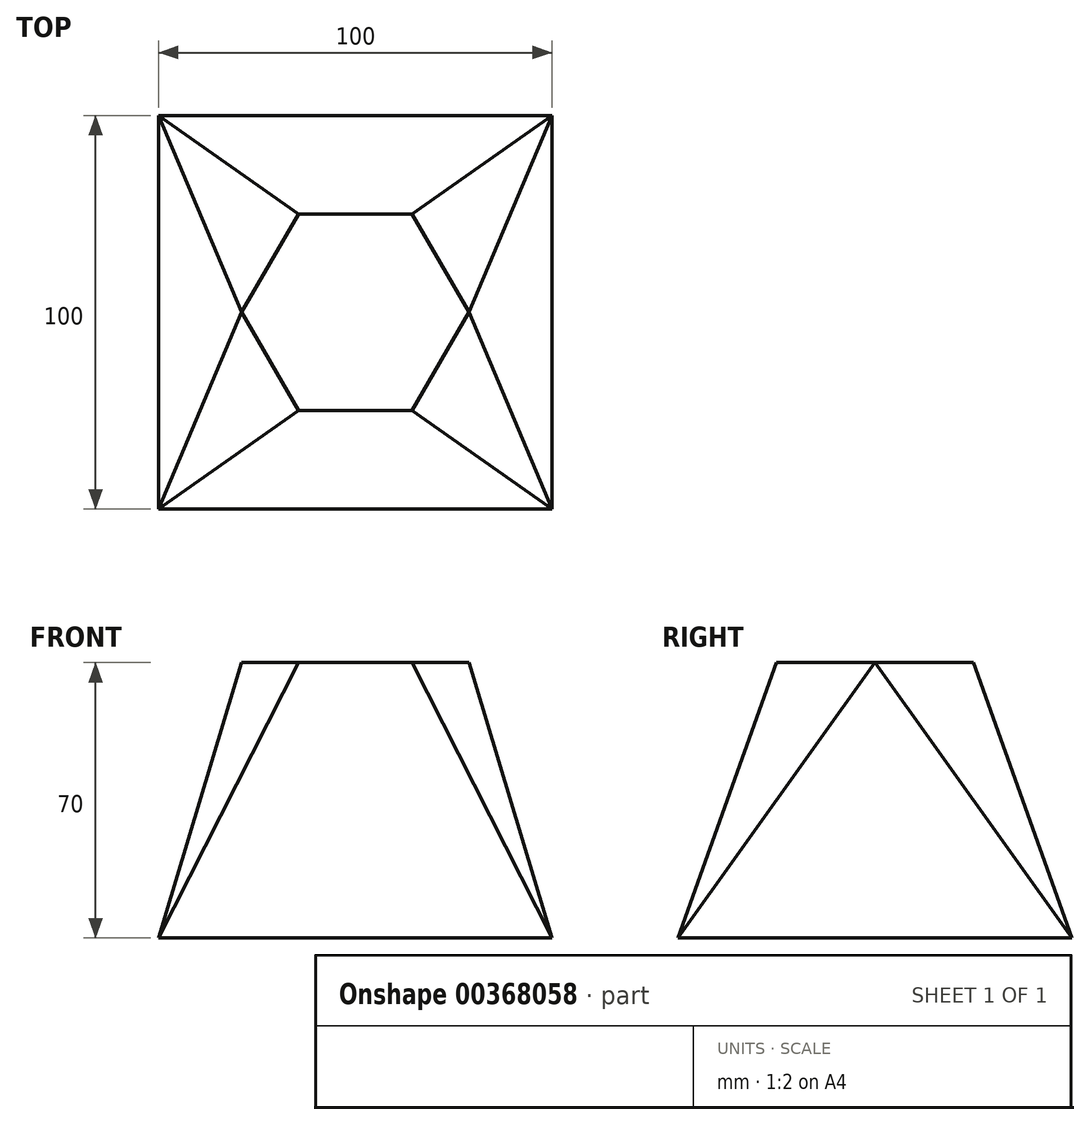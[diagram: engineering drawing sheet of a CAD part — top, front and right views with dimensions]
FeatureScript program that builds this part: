
annotation { "Feature Type Name" : "Feature", "Feature Type Description" : "" }
export const myFeature = defineFeature(function(context is Context, id is Id, definition is map)
    precondition{}
    {
        {
            var Q0;
            Q0=qCreatedBy(makeId("Top.planeOp"),FACE);
            var sketch = newSketch(context, id + "F0", { "sketchPlane" : qUnion([Q0])});
            skLineSegment(sketch, "E0.bottom", {"start": v(-50, 50) * mm, "end": v(50, 50) * mm});
            skLineSegment(sketch, "E0.top", {"start": v(-50, -50) * mm, "end": v(50, -50) * mm});
            skLineSegment(sketch, "E0.left", {"start": v(-50, 50) * mm, "end": v(-50, -50) * mm});
            skLineSegment(sketch, "E0.right", {"start": v(50, 50) * mm, "end": v(50, -50) * mm});
            skPoint(sketch, "E0.middle", {"position": v(0, 0) * mm});
            skSolve(sketch);
        }
        {
            var Q0;
            Q0=qCreatedBy(makeId("Top.planeOp"),FACE);
            cPlane(context, id + "F1", {"entities" : qUnion([Q0]), "cplaneType" : CPlaneType.OFFSET, "offset" : 70 * mm, "width" : 150 * mm, "height" : 150 * mm});
        }
        {
            var Q0;
            Q0=qCreatedBy(id+"F1.planeOp",FACE);
            var sketch = newSketch(context, id + "F2", { "sketchPlane" : qUnion([Q0])});
            skCircle(sketch, "E1.cCircle", {"center": v(0, 0) * mm, "radius": 25 * mm, "construction": true});
            skLineSegment(sketch, "E1.0", {"start": v(-14.43, 25) * mm, "end": v(14.43, 25) * mm});
            skLineSegment(sketch, "E1.1", {"start": v(14.43, 25) * mm, "end": v(28.87, 0) * mm});
            skLineSegment(sketch, "E1.2", {"start": v(28.87, 0) * mm, "end": v(14.43, -25) * mm});
            skLineSegment(sketch, "E1.3", {"start": v(14.43, -25) * mm, "end": v(-14.43, -25) * mm});
            skLineSegment(sketch, "E1.4", {"start": v(-14.43, -25) * mm, "end": v(-28.87, 0) * mm});
            skLineSegment(sketch, "E1.5", {"start": v(-28.87, 0) * mm, "end": v(-14.43, 25) * mm});
            skPoint(sketch, "E1.0.midPoint", {"position": v(0, 25) * mm});
            skLineSegment(sketch, "E2", {"start": v(-14.43, 25) * mm, "end": v(-14.43, -25) * mm});
            skLineSegment(sketch, "E3", {"start": v(14.43, 25) * mm, "end": v(14.43, -25) * mm});
            skSolve(sketch);
        }
        {
            var Q0;
            Q0=makeQuery(id+"F0.imprint","IMPRINT",FACE,{"disambiguationData":[TD([[makeQuery(id+"F0.imprint","IMPRINT",EDGE,{"derivedFrom":sQuery(id+"F0.wireOp",EDGE,"E0.bottom")}),-1.0]])]});
            var Q1;
            Q1=makeQuery(id+"F2.imprint","IMPRINT",FACE,{"disambiguationData":[TD([[makeQuery(id+"F2.imprint","IMPRINT",EDGE,{"derivedFrom":sQuery(id+"F2.wireOp",EDGE,"E1.0")}),-1.0]])]});
            loft(context, id + "F3", {"sheetProfilesArray" : [{ "sheetProfileEntities" : qUnion([Q0]) }, { "sheetProfileEntities" : qUnion([Q1]) }]});
        }
        {
            var Q1;
            Q1=makeQuery(id+"F2.imprint","IMPRINT",FACE,{"disambiguationData":[TD([[makeQuery(id+"F2.imprint","IMPRINT",EDGE,{"derivedFrom":sQuery(id+"F2.wireOp",EDGE,"E1.4")}),-1.0]])]});
            var Q2;
            Q2=makeQuery(id+"F3.opLoft","MID_CAP_VERTEX",VERTEX,{"disambiguationData":[OSD([sQuery(id+"F0.wireOp",EDGE,"E0.bottom"),sQuery(id+"F0.wireOp",EDGE,"E0.left")])],"capPos":0.0});
            loft(context, id + "F4", {"operationType" : NewBodyOperationType.ADD, "sheetProfilesArray" : [{ "sheetProfileEntities" : qUnion([Q1]) }, { "sheetProfileEntities" : qUnion([Q2]) }]});
        }
        {
            var Q1;
            Q1=makeQuery(id+"F2.imprint","IMPRINT",FACE,{"disambiguationData":[TD([[makeQuery(id+"F2.imprint","IMPRINT",EDGE,{"derivedFrom":sQuery(id+"F2.wireOp",EDGE,"E1.4")}),-1.0]])]});
            var Q2;
            Q2=makeQuery(id+"F3.opLoft","MID_CAP_VERTEX",VERTEX,{"disambiguationData":[OSD([sQuery(id+"F0.wireOp",EDGE,"E0.top"),sQuery(id+"F0.wireOp",EDGE,"E0.left")])],"capPos":0.0});
            loft(context, id + "F5", {"operationType" : NewBodyOperationType.ADD, "sheetProfilesArray" : [{ "sheetProfileEntities" : qUnion([Q1]) }, { "sheetProfileEntities" : qUnion([Q2]) }]});
        }
        {
            var Q1;
            Q1=makeQuery(id+"F4.opLoft","SWEPT_FACE",FACE,{"disambiguationData":[OSD([sQuery(id+"F2.wireOp",EDGE,"E1.3"),sQuery(id+"F2.wireOp",EDGE,"E1.4"),sQuery(id+"F2.wireOp",EDGE,"E1.5"),sQuery(id+"F2.wireOp",EDGE,"E2")])]});
            var Q2;
            Q2=makeQuery(id+"F5.opLoft","SWEPT_FACE",FACE,{"disambiguationData":[OSD([sQuery(id+"F2.wireOp",EDGE,"E1.0"),sQuery(id+"F2.wireOp",EDGE,"E1.4"),sQuery(id+"F2.wireOp",EDGE,"E1.5"),sQuery(id+"F2.wireOp",EDGE,"E2")])]});
            var Q3;
            {var subQ0=sQuery(id+"F0.wireOp",EDGE,"E0.left");var subQ1=sQuery(id+"F0.wireOp",EDGE,"E0.bottom");Q3=makeQuery(id+"F4.boolean.opBoolean","MERGE",VERTEX,{"derivedFrom":[makeQuery(id+"F3.opLoft","MID_CAP_VERTEX",VERTEX,{"disambiguationData":[OSD([subQ1,subQ0])],"capPos":0.0}),makeQuery(id+"F4.opLoft","SWEPT_VERTEX",VERTEX,{"disambiguationData":[OSD([subQ1,subQ0,sQuery(id+"F2.wireOp",EDGE,"E1.3"),sQuery(id+"F2.wireOp",EDGE,"E1.4"),sQuery(id+"F2.wireOp",EDGE,"E2")])]})]});}
            var Q4;
            {var subQ0=sQuery(id+"F0.wireOp",EDGE,"E0.left");var subQ1=sQuery(id+"F0.wireOp",EDGE,"E0.top");Q4=makeQuery(id+"F5.boolean.opBoolean","MERGE",VERTEX,{"derivedFrom":[makeQuery(id+"F3.opLoft","MID_CAP_VERTEX",VERTEX,{"disambiguationData":[OSD([subQ1,subQ0])],"capPos":0.0}),makeQuery(id+"F5.opLoft","SWEPT_VERTEX",VERTEX,{"disambiguationData":[OSD([subQ1,subQ0,sQuery(id+"F2.wireOp",EDGE,"E1.3"),sQuery(id+"F2.wireOp",EDGE,"E1.4"),sQuery(id+"F2.wireOp",EDGE,"E2")])]})]});}
            loft(context, id + "F6", {"operationType" : NewBodyOperationType.ADD, "sheetProfilesArray" : [{ "sheetProfileEntities" : qUnion([Q1]) }, { "sheetProfileEntities" : qUnion([Q2]) }], "matchConnections" : true, "connections" : [{ "connectionEntities" : qUnion([Q3, Q4]), "connectionEdgeQueries" : qUnion([]), "connectionEdgeParameters" : [] }]});
        }
        {
            var Q1;
            Q1=makeQuery(id+"F2.imprint","IMPRINT",FACE,{"disambiguationData":[TD([[makeQuery(id+"F2.imprint","IMPRINT",EDGE,{"derivedFrom":sQuery(id+"F2.wireOp",EDGE,"E1.1")}),-1.0]])]});
            var Q2;
            Q2=makeQuery(id+"F3.opLoft","MID_CAP_VERTEX",VERTEX,{"disambiguationData":[OSD([sQuery(id+"F0.wireOp",EDGE,"E0.top"),sQuery(id+"F0.wireOp",EDGE,"E0.right")])],"capPos":0.0});
            loft(context, id + "F7", {"operationType" : NewBodyOperationType.ADD, "sheetProfilesArray" : [{ "sheetProfileEntities" : qUnion([Q1]) }, { "sheetProfileEntities" : qUnion([Q2]) }]});
        }
        {
            var Q1;
            Q1=makeQuery(id+"F2.imprint","IMPRINT",FACE,{"disambiguationData":[TD([[makeQuery(id+"F2.imprint","IMPRINT",EDGE,{"derivedFrom":sQuery(id+"F2.wireOp",EDGE,"E1.1")}),-1.0]])]});
            var Q2;
            Q2=makeQuery(id+"F3.opLoft","MID_CAP_VERTEX",VERTEX,{"disambiguationData":[OSD([sQuery(id+"F0.wireOp",EDGE,"E0.bottom"),sQuery(id+"F0.wireOp",EDGE,"E0.right")])],"capPos":0.0});
            loft(context, id + "F8", {"operationType" : NewBodyOperationType.ADD, "sheetProfilesArray" : [{ "sheetProfileEntities" : qUnion([Q1]) }, { "sheetProfileEntities" : qUnion([Q2]) }]});
        }
        {
            var Q1;
            Q1=makeQuery(id+"F7.opLoft","SWEPT_FACE",FACE,{"disambiguationData":[OSD([sQuery(id+"F2.wireOp",EDGE,"E1.0"),sQuery(id+"F2.wireOp",EDGE,"E1.1"),sQuery(id+"F2.wireOp",EDGE,"E1.2"),sQuery(id+"F2.wireOp",EDGE,"E3")])]});
            var Q2;
            Q2=makeQuery(id+"F8.opLoft","SWEPT_FACE",FACE,{"disambiguationData":[OSD([sQuery(id+"F2.wireOp",EDGE,"E1.1"),sQuery(id+"F2.wireOp",EDGE,"E1.2"),sQuery(id+"F2.wireOp",EDGE,"E1.3"),sQuery(id+"F2.wireOp",EDGE,"E3")])]});
            var Q3;
            {var subQ0=sQuery(id+"F0.wireOp",EDGE,"E0.right");var subQ1=sQuery(id+"F0.wireOp",EDGE,"E0.top");Q3=makeQuery(id+"F7.boolean.opBoolean","MERGE",VERTEX,{"derivedFrom":[makeQuery(id+"F3.opLoft","MID_CAP_VERTEX",VERTEX,{"disambiguationData":[OSD([subQ1,subQ0])],"capPos":0.0}),makeQuery(id+"F7.opLoft","SWEPT_VERTEX",VERTEX,{"disambiguationData":[OSD([subQ1,subQ0,sQuery(id+"F2.wireOp",EDGE,"E1.1"),sQuery(id+"F2.wireOp",EDGE,"E1.2")])]})]});}
            var Q4;
            {var subQ0=sQuery(id+"F0.wireOp",EDGE,"E0.right");var subQ1=sQuery(id+"F0.wireOp",EDGE,"E0.bottom");Q4=makeQuery(id+"F8.boolean.opBoolean","MERGE",VERTEX,{"derivedFrom":[makeQuery(id+"F3.opLoft","MID_CAP_VERTEX",VERTEX,{"disambiguationData":[OSD([subQ1,subQ0])],"capPos":0.0}),makeQuery(id+"F8.opLoft","SWEPT_VERTEX",VERTEX,{"disambiguationData":[OSD([subQ1,subQ0,sQuery(id+"F2.wireOp",EDGE,"E1.1"),sQuery(id+"F2.wireOp",EDGE,"E1.2")])]})]});}
            loft(context, id + "F9", {"operationType" : NewBodyOperationType.ADD, "sheetProfilesArray" : [{ "sheetProfileEntities" : qUnion([Q1]) }, { "sheetProfileEntities" : qUnion([Q2]) }], "matchConnections" : true, "connections" : [{ "connectionEntities" : qUnion([Q3, Q4]), "connectionEdgeQueries" : qUnion([]), "connectionEdgeParameters" : [] }]});
        }
    });
